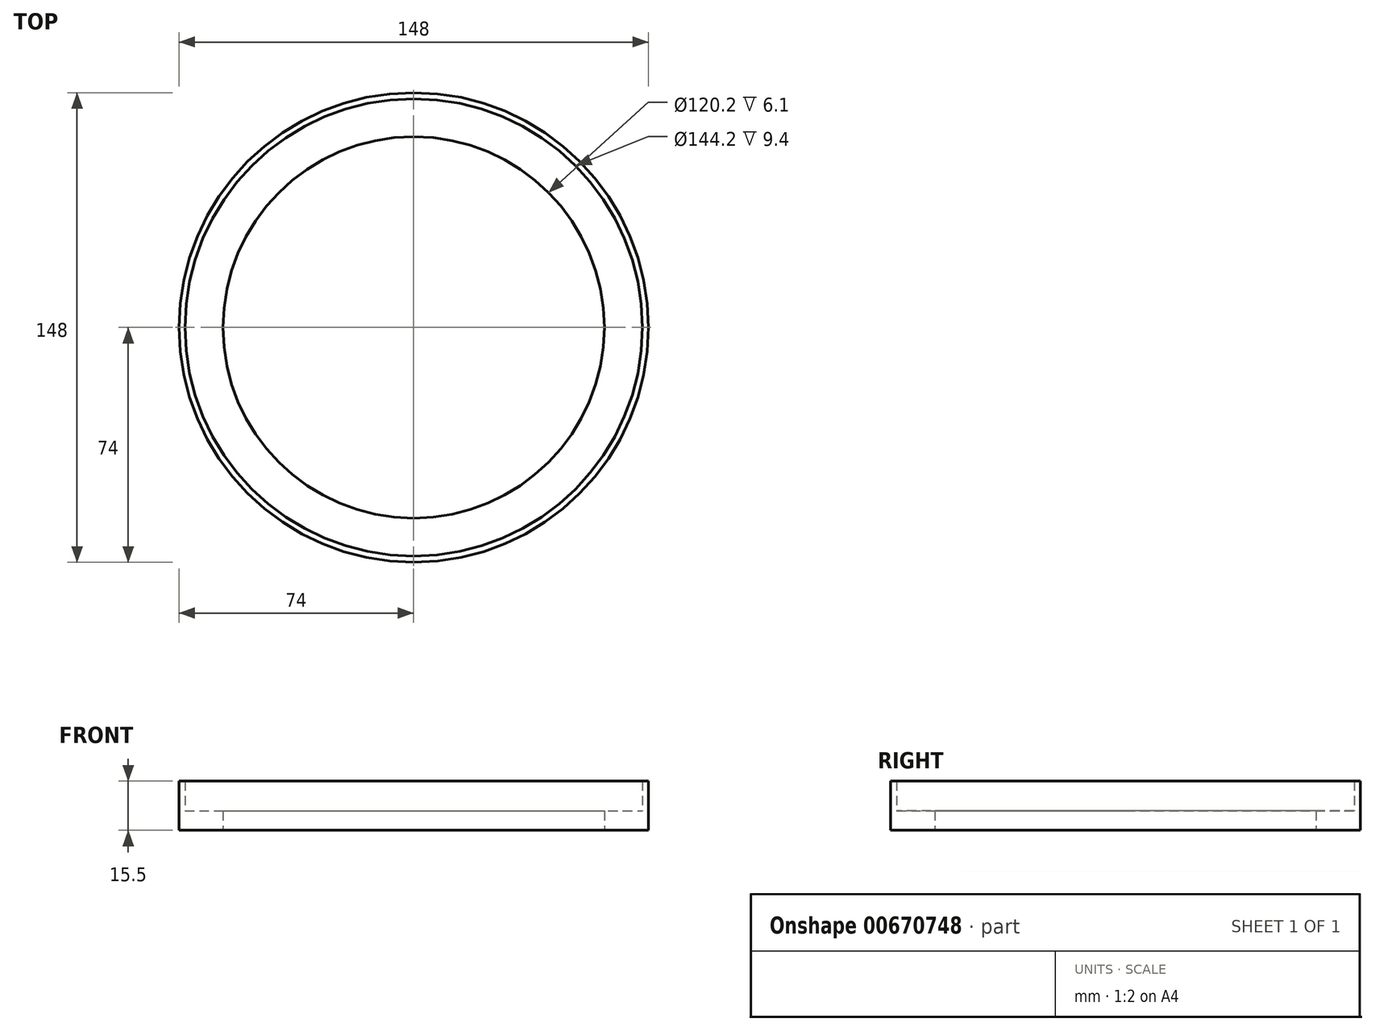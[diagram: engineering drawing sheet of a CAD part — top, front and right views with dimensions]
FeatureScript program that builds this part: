
annotation { "Feature Type Name" : "Feature", "Feature Type Description" : "" }
export const myFeature = defineFeature(function(context is Context, id is Id, definition is map)
    precondition{}
    {
        {
            var Q0;
            Q0=qCreatedBy(makeId("Front.planeOp"),FACE);
            var sketch = newSketch(context, id + "F0", { "sketchPlane" : qUnion([Q0])});
            skLineSegment(sketch, "E0", {"start": v(60.1, 0) * mm, "end": v(74, 0) * mm});
            skLineSegment(sketch, "E1", {"start": v(74, 0) * mm, "end": v(74, 15.5) * mm});
            skLineSegment(sketch, "E2", {"start": v(74, 15.5) * mm, "end": v(72.1, 15.5) * mm});
            skLineSegment(sketch, "E3", {"start": v(72.1, 15.5) * mm, "end": v(72.1, 6.1) * mm});
            skLineSegment(sketch, "E4", {"start": v(72.1, 6.1) * mm, "end": v(60.1, 6.1) * mm});
            skLineSegment(sketch, "E5", {"start": v(60.1, 6.1) * mm, "end": v(60.1, 0) * mm});
            skLineSegment(sketch, "E6", {"start": v(0, 0) * mm, "end": v(0, 16.73) * mm, "construction": true});
            skSolve(sketch);
        }
        {
            var Q0;
            Q0=makeQuery(id+"F0.imprint","IMPRINT",FACE,{"disambiguationData":[TD([[makeQuery(id+"F0.imprint","IMPRINT",EDGE,{"derivedFrom":sQuery(id+"F0.wireOp",EDGE,"E0")}),1.0]])]});
            var Q1;
            Q1=sQuery(id+"F0.wireOp",EDGE,"E6");
            revolve(context, id + "F1", {"entities" : qUnion([Q0]), "axis" : qUnion([Q1]), "revolveType" : RevolveType.FULL});
        }
    });
